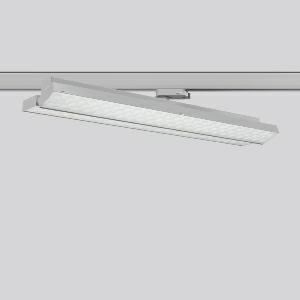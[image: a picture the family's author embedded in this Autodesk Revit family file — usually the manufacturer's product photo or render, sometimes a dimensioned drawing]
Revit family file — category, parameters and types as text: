
# Revit family: tx-move_742162_004_1_76_03ab
name_source: partatom
category: Lighting Fixtures
units: mm (PartAtom-declared; Revit-internal decimal feet)

## family parameters
Cut with Voids When Loaded = No
Host = Face
Light Source = No
Part Type = Normal
Room Calculation Point = No
Round Connector Dimension = Use Diameter
Shared = No

## types (1)
- MultiLumen 1 (1 x LED Modul 840, 3150 lm, 4000)
    Apparent Load = 41 VA
    CIE Flux Codes = 77 96 99 100 100
    Color Rendering = 80
    Color Temperature = 4000
    Default Elevation = 1800 mm
    Description = Series: TX-MOVE
Multifunctional surface-mounted spotlight for area lighting. Very flat design. Housing: sheet steel, powder-coated. Rotation range: 356°. Swivel range: 90°. Consistent alignment possible with visible tilt scale. High-efficiency LED units with optimum light control thanks to clear plastic (PC) lens optics. Spezielle Mikrostrukturen reduzieren Gelbsaum. Symmetrical light distribution. With adapter for RZB 3-circuit DALI tracks. Suitable for Track on ceiling. MultiLumen: Luminous flux adjustable in 3 steps. Factory setting is the highest luminous flux. Environmentally friendly and resource-saving due to replaceable and recyclable components. 
Colour: silver, matt (approx. RAL 9006)
Length: 570 mm
Width: 119 mm
Height: 88 mm
Lamp: LED
Socket: without socket
Colour temperature: 4000K
Colour rendering index (CRI): 80
System power: 41 W
Rated luminous flux: 6300 lm
Luminous efficiency: 154 lm/W
System power 2: 57 W
Rated luminous flux 2: 8550 lm
Luminous efficiency 2: 150 lm/W
System power 3: 73 W
Rated luminous flux 3: 10400 lm
Luminous efficiency 3: 142 lm/W
Control gear: Dimmable EVG, DALI
Protection class: I
Type of protection: IP 20
    Height = 75 mm
    Lamp = 1 x LED Modul 840
    Lamp Light Flux = 3150 lm
    Lamp count = 1
    Length = 569 mm
    Lifetime = 50000 h
    Luminous efficacy = 154 lm/W
    Manufacturer = RZB
    ModVariant = No
    Model = 742162.004.1.76
    Mounting Place = Ceiling
    Mounting Type = Surface mounted
    Number of Poles = 1
    OnlyDefault = Yes
    Power Factor = 1
    Product Name = TX-MOVE
    Product group = Track mounted projectors
    ProductGroupID = 301
    Protection Class = Protection class I
    Protection Degree = IP 20
    RLX_Detail_Level = 1
    RLX_Emergency_Light_Flux = 0 lm
    RLX_Emergency_Type = 0
    RLX_Emergency_Type_DB = No
    RlxData = <blob elided: 33217 chars, md5=1da24cf4>
    Socket = socket
    Standby Power = 0 W
    System Light Flux = 6300 lm
    System Power = 41 W
    Type Comments = MultiLumen 1
    Type Image = 742162.004.jpg
    URL = http://relux.com
    VarID = multilumen_1
    Voltage = 0 V
    Weight = 0.00 kg
    Width = 119 mm

## geometry (parser evidence)
native form markers: Blend x4, Sweep x15
no freeform markers — native parametric forms only
